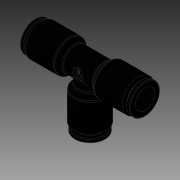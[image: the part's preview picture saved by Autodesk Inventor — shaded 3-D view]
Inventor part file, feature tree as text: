
AUTODESK INVENTOR PART (.ipt)
format: ipt  version: 2016 SP1 (Build 200210100, 210)  size: 257,536 bytes
history: native  units: in
note: dims shown in document units (in); Inventor stores cm internally (conversion verified against a paired STEP export)
features: extrude x2, sketch x2
ambient origin geometry x8: Origin, YZ Plane, XZ Plane, XY Plane, X Axis, Y Axis, Z Axis, Center Point
bodies: Solid1 (feature_tree)
feature tree (4):
  extrude  "Extrusion1"  Depth=1.0in TaperAngle=0.0deg
  extrude  "Extrusion2"  Depth=0.578in TaperAngle=0.0deg
  sketch  "Sketch1"  dims[d0=0.25in d1=1.0in d2=0.0in]
  sketch  "Sketch2"  dims[d3=0.25in d4=0.578in d5=0.0in]
